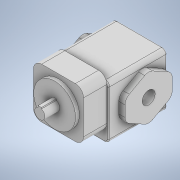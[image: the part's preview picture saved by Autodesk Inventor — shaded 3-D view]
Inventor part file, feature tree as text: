
AUTODESK INVENTOR PART (.ipt)
format: ipt  version: 2020 (Build 240168000, 168)  size: 269,824 bytes
history: native  units: mm
features: extrude x9, sketch x9, plane x2, fillet x2
ambient origin geometry x8: Origin, YZ Plane, XZ Plane, XY Plane, X Axis, Y Axis, Z Axis, Center Point
bodies: Solid1 (feature_tree)
feature tree (22):
  extrude  "Extrusion1"  Depth=130.0mm
  plane  "Work Plane2"
  extrude  "Extrusion2"  Depth=65.0mm
  sketch  "Sketch3"  dims[d4=203.2mm d5=0.0mm d8=50.0mm]
  plane  "Work Plane1"
  extrude  "Extrusion3"  Depth=50.0mm
  extrude  "Extrusion4"  Depth=130.0mm
  extrude  "Extrusion5"  Depth=15.0mm TaperAngle=0.0deg
  fillet  "Fillet8"  Radius=31.6mm
  extrude  "Extrusion6"  Depth=115.3mm
  fillet  "Fillet9"  Radius=40.0mm
  extrude  "Extrusion7"  Depth=15.0mm TaperAngle=0.0deg
  extrude  "Extrusion8"  Depth=160.0mm TaperAngle=0.0deg
  extrude  "Extrusion9"  Depth=10.0mm
  sketch  "Sketch1"  dims[d0=130.0mm d1=130.0mm]
  sketch  "Sketch2"  dims[d2=65.0mm d3=65.0mm]
  sketch  "Sketch4"  dims[d9=115.0mm d10=130.0mm]
  sketch  "Sketch6"  dims[d11=40.0mm d12=15.0mm d13=0.0mm d18=31.6mm]
  sketch  "Sketch7"  dims[d19=115.3mm d20=50.0mm d21=40.0mm]
  sketch  "Sketch8"  dims[d22=130.0mm d23=15.0mm d24=0.0mm]
  sketch  "Sketch9"  dims[d27=160.0mm d28=0.0mm d33=60.9mm d34=0.0mm]
  sketch  "Sketch10"  dims[d35=3.0mm d36=10.0mm d37=20.0mm d38=122.0mm d39=122.0mm d40=4.0mm d41=22.5mm d42=56.5mm d43=0.0mm d44=20.0mm d45=101.6mm d46=61.0mm d47=9.4mm d48=0.0mm d49=25.0mm d50=36.1mm d51=0.0mm d52=8.0mm d53=5.0mm d54=2.5mm d55=4.0mm d56=36.1mm d57=0.0mm d6=0.5mm d7=0.872665mm d58=0.5mm d59=0.872665mm]
